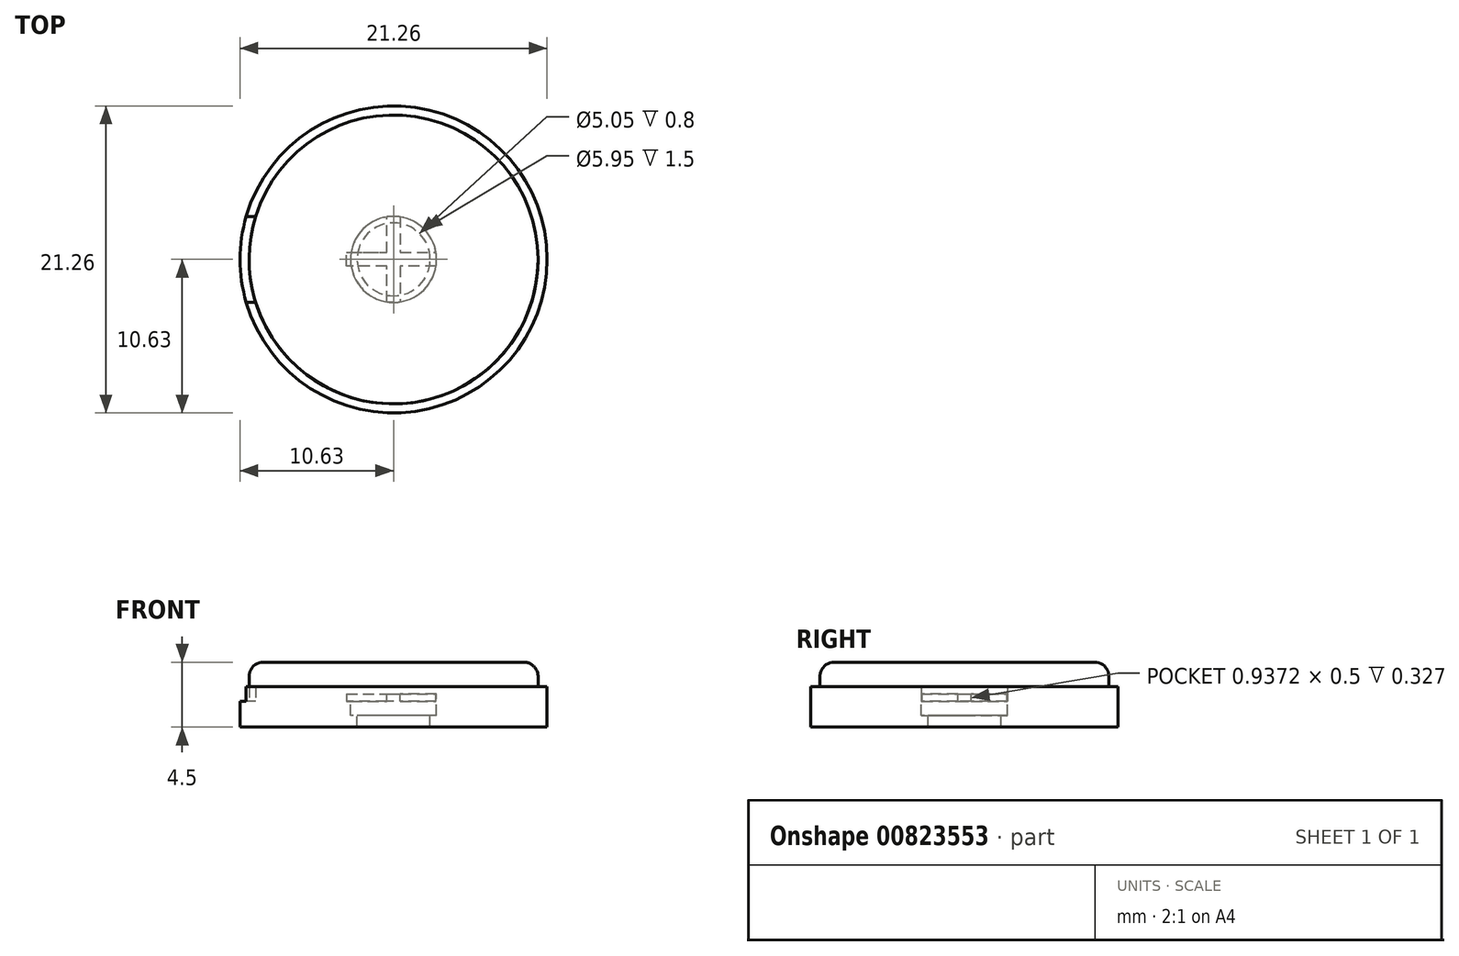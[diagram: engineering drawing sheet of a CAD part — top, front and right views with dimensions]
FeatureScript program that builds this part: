
annotation { "Feature Type Name" : "Feature", "Feature Type Description" : "" }
export const myFeature = defineFeature(function(context is Context, id is Id, definition is map)
    precondition{}
    {
        {
            var Q0;
            Q0=qCreatedBy(makeId("Top.planeOp"),FACE);
            var sketch = newSketch(context, id + "F0", { "sketchPlane" : qUnion([Q0])});
            skCircle(sketch, "E0", {"center": v(0, 0) * mm, "radius": 10.63 * mm});
            skCircle(sketch, "E1", {"center": v(0, 0) * mm, "radius": 10 * mm});
            skCircle(sketch, "E2", {"center": v(0, 0) * mm, "radius": 2.52 * mm});
            skSolve(sketch);
        }
        {
            var Q0;
            Q0=makeQuery(id+"F0.imprint","IMPRINT",FACE,{"disambiguationData":[TD([[makeQuery(id+"F0.imprint","IMPRINT",EDGE,{"derivedFrom":sQuery(id+"F0.wireOp",EDGE,"E0")}),1.0]])]});
            var Q1;
            Q1=makeQuery(id+"F0.imprint","IMPRINT",FACE,{"disambiguationData":[TD([[makeQuery(id+"F0.imprint","IMPRINT",EDGE,{"derivedFrom":sQuery(id+"F0.wireOp",EDGE,"E1")}),1.0]])]});
            extrude(context, id + "F1", {"entities" : qUnion([Q0, Q1]), "oppositeDirection" : true, "depth" : 1.8 * mm, "offsetDistance" : 25 * mm});
        }
        {
            var Q0;
            Q0=makeQuery(id+"F0.imprint","IMPRINT",FACE,{"disambiguationData":[TD([[makeQuery(id+"F0.imprint","IMPRINT",EDGE,{"derivedFrom":sQuery(id+"F0.wireOp",EDGE,"E1")}),1.0]])]});
            var Q1;
            Q1=makeQuery(id+"F0.imprint","IMPRINT",FACE,{"disambiguationData":[TD([[makeQuery(id+"F0.imprint","IMPRINT",EDGE,{"derivedFrom":sQuery(id+"F0.wireOp",EDGE,"E2")}),1.0]])]});
            extrude(context, id + "F2", {"entities" : qUnion([Q0, Q1]), "depth" : 2.7 * mm, "offsetDistance" : 25 * mm});
        }
        {
            var Q0;
            Q0=makeQuery(id+"F2.opExtrude","CAP_EDGE",EDGE,{"disambiguationData":[OSD([sQuery(id+"F0.wireOp",EDGE,"E1")])],"isStart":false});
            fillet(context, id + "F3", {"entities" : qUnion([Q0]), "radius" : 1 * mm, "tangentPropagation" : true, "allowEdgeOverflow" : false});
        }
        {
            var Q0;
            Q0=makeQuery(id+"F0.imprint","IMPRINT",FACE,{"disambiguationData":[TD([[makeQuery(id+"F0.imprint","IMPRINT",EDGE,{"derivedFrom":sQuery(id+"F0.wireOp",EDGE,"E1")}),1.0]])]});
            var sketch = newSketch(context, id + "F4", { "sketchPlane" : qUnion([Q0])});
            skCircle(sketch, "E3.0", {"center": v(0, 0) * mm, "radius": 10 * mm});
            skText(sketch, "E4", { "text": "+", "fontName": "OpenSans-Regular.ttf"});
            const initialGuessF4  = {"E4": [-0.00397, -0.0049, 1, 0, 0.01002]};
            skSetInitialGuess(sketch, initialGuessF4);
            skSolve(sketch);
        }
        {
            var Q0;
            {var subQ0=sQuery(id+"F4.wireOp",EDGE,"E4.sketch_text.stroke-4");Q0=makeQuery(id+"F4.imprint","IMPRINT",FACE,{"disambiguationData":[TD([[makeQuery(id+"F4.imprint","IMPRINT",EDGE,{"derivedFrom":subQ0}),-1.0]])]});}
            var Q1;
            {var subQ0=sQuery(id+"F4.wireOp",EDGE,"E4.sketch_text.stroke-7");Q1=makeQuery(id+"F4.imprint","IMPRINT",FACE,{"disambiguationData":[TD([[makeQuery(id+"F4.imprint","IMPRINT",EDGE,{"derivedFrom":subQ0}),-1.0]])]});}
            var Q2;
            {var subQ0=sQuery(id+"F4.wireOp",EDGE,"E4.sketch_text.stroke-10");Q2=makeQuery(id+"F4.imprint","IMPRINT",FACE,{"disambiguationData":[TD([[makeQuery(id+"F4.imprint","IMPRINT",EDGE,{"derivedFrom":subQ0}),-1.0]])]});}
            var Q3;
            {var subQ0=sQuery(id+"F4.wireOp",EDGE,"E4.sketch_text.stroke-1");Q3=makeQuery(id+"F4.imprint","IMPRINT",FACE,{"disambiguationData":[TD([[makeQuery(id+"F4.imprint","IMPRINT",EDGE,{"derivedFrom":subQ0}),-1.0]])]});}
            var Q4;
            {var subQ5=sQuery(id+"F4.wireOp",EDGE,"E4.sketch_text.stroke-11");var subQ6=sQuery(id+"F4.wireOp",EDGE,"E4.sketch_text.stroke-0");var subQ7=makeQuery(id+"F4.imprint","INTERSECT",VERTEX,{"derivedFrom":[subQ6,subQ5]});Q4=makeQuery(id+"F4.imprint","IMPRINT",FACE,{"disambiguationData":[TD([[makeQuery(id+"F4.imprint","IMPRINT",EDGE,{"disambiguationData":[TD([[subQ7,-1.0]])],"derivedFrom":subQ6}),-1.0]])]});}
            extrude(context, id + "F5", {"entities" : qUnion([Q0, Q1, Q2, Q3, Q4]), "operationType" : NewBodyOperationType.REMOVE, "depth" : .5 * mm, "offsetDistance" : 25 * mm});
        }
        {
            var Q0;
            Q0=makeQuery(id+"F1.opExtrude","CAP_FACE",FACE,{"disambiguationData":[OSD([sQuery(id+"F0.wireOp",EDGE,"E0"),sQuery(id+"F0.wireOp",EDGE,"E2")])],"isStart":true});
            var sketch = newSketch(context, id + "F6", { "sketchPlane" : qUnion([Q0])});
            skCircle(sketch, "E5", {"center": v(0, 0) * mm, "radius": 2.97 * mm});
            skSolve(sketch);
        }
        {
            var Q0;
            Q0 = qSketchRegion(id + "F6", true);
            extrude(context, id + "F7", {"entities" : qUnion([Q0]), "operationType" : NewBodyOperationType.REMOVE, "oppositeDirection" : true, "depth" : 1 * mm, "offsetDistance" : 25 * mm});
        }
        {
            var Q0;
            Q0=makeQuery(id+"F1.opExtrude","SWEPT_BODY",BODY,{"disambiguationData":[OSD([sQuery(id+"F0.wireOp",EDGE,"E0"),sQuery(id+"F0.wireOp",EDGE,"E2")])]});
            transform(context, id + "F8", {"entities" : qUnion([Q0]), "transformType" : TransformType.TRANSLATION_3D, "dx" : 0 * mm, "dy" : 0 * mm, "dz" : 0 * mm, "makeCopy" : true});
        }
        {
            var Q0;
            Q0=makeQuery(id+"F8.opPattern","COPY",FACE,{"derivedFrom":makeQuery(id+"F1.opExtrude","CAP_FACE",FACE,{"disambiguationData":[OSD([sQuery(id+"F0.wireOp",EDGE,"E0"),sQuery(id+"F0.wireOp",EDGE,"E2")])],"isStart":true}),"instanceName":"1"});
            var sketch = newSketch(context, id + "F9", { "sketchPlane" : qUnion([Q0])});
            skArc(sketch, "E6.0", {"start": v(-10.2, -2.98) * mm, "mid": v(10.63, 0) * mm, "end": v(-10.2, 2.98) * mm});
            skArc(sketch, "E7.0", {"start": v(0, -2.97) * mm, "mid": v(2.97, 0) * mm, "end": v(0, 2.97) * mm});
            skLineSegment(sketch, "E8.bottom", {"start": v(0, 2.98) * mm, "end": v(-10.2, 2.97) * mm});
            skLineSegment(sketch, "E8.top", {"start": v(0, -2.97) * mm, "end": v(-10.2, -2.98) * mm});
            skSolve(sketch);
        }
        {
            var Q0;
            Q0 = qSketchRegion(id + "F9", true);
            extrude(context, id + "F10", {"entities" : qUnion([Q0]), "operationType" : NewBodyOperationType.ADD, "depth" : 1 * mm, "offsetDistance" : 25 * mm});
        }
    });
